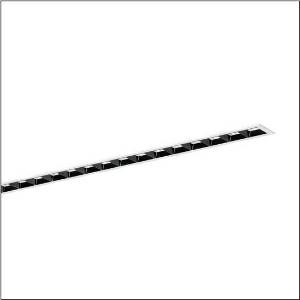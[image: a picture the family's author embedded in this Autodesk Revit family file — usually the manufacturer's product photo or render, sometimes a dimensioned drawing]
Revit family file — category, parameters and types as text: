
# Revit family: silica_r__21_51mx12dc3awb_9b9c
name_source: partatom
category: Lighting Fixtures
units: mm (PartAtom-declared; Revit-internal decimal feet)

## family parameters
Cut with Voids When Loaded = No
Host = Face
Light Source = No
Part Type = Normal
Room Calculation Point = No
Round Connector Dimension = Use Diameter
Shared = No

## types (1)
- --- (1 x LED, 10800 lm, 69.2 W, 3000K)
    Apparent Load = 69 VA
    CIE Flux Codes = 86 100 100 100 100
    Color Rendering = 80
    Color Temperature = 3000K
    Default Elevation = 1800 mm
    Description = Silica® 21, office luminaire, primary light control with darklight reflector, of PMMA, black, CAT 2 (L<= 3000cd/m²), light emission: direct distribution, primary light characteristic: symmetric, installation type: recessed, LED, rated luminous flux: 10.800lm, luminous efficacy: 156lm/W, light colour: 830, colour temperature: 3000K, control gear: DALI 2, with terminal, 3+2-pole, max. 2.5mm², mains connection: 220..240V, AC, 50/60Hz, rated input power: 69.2W, luminaire housing, of aluminium, traffic white (RAL 9016), length: 3.028mm, width: 79mm, height: 53mm, protection rating (complete): IP20, insulation class (complete): insulation class I (protective earthing), certification: CE, ENEC, VDE, permissible operating ambient temperature: 0..+35°C, standard: EN 50419, packaging unit: 1 piece
    Height = 0 mm  [stored 0 ft]
    Lamp = 1 x LED
    Lamp Light Flux = 10800 lm
    Lamp Power = 69.2 W
    Lamp count = 1
    Length = 3027 mm
    Luminous efficacy = 156 lm/W
    Manufacturer = Siteco
    ModVariant = No
    Model = 51MX12DC3AWB
    Mounting Place = Ceiling
    Mounting Type = Recessed
    Number of Poles = 1
    OnlyDefault = Yes
    Power Factor = 1
    Product Name = Silica® 21
    Product group = office luminaire | ceiling recessed
    ProductGroupID = 401
    Protection Class = Protection class I
    Protection Degree = IP 20
    RLX_Detail_Level = 1
    RLX_Emergency_Light_Flux = 0 lm
    RLX_Emergency_Type = 0
    RLX_Emergency_Type_DB = No
    RlxData = <blob elided: 63041 chars, md5=c520fc7e>
    Socket = socket
    Standby Power = 0 W
    System Light Flux = 10800 lm
    System Power = 69 W
    Type Comments = factory setting: luminous flux: 100 % | dim-lin: 254 | 392 mA
    Type Image = l_1335880.jpg
    URL = http://relux.com
    VarID = @adj_124336
    Voltage = 0 V
    Weight = 0.00 kg
    Width = 79 mm

note: [stored X ft] marks values corroborated as IEEE doubles in the binary element streams (Revit-internal decimal feet)

## geometry (parser evidence)
native form markers: Blend x4, Sweep x10
no freeform markers — native parametric forms only
